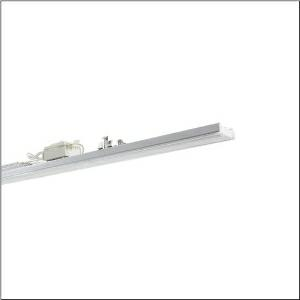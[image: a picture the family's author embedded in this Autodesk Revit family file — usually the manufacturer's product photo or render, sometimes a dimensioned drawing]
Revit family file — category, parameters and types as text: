
# Revit family: licross_r__11_recessed_ho_51tl11dn4exs_1c00
name_source: partatom
category: Lighting Fixtures
units: mm (PartAtom-declared; Revit-internal decimal feet)

## family parameters
Cut with Voids When Loaded = No
Host = Face
Light Source = No
Part Type = Normal
Room Calculation Point = No
Round Connector Dimension = Use Diameter
Shared = No

## types (1)
- --- (1 x LED, 14000 lm, 76.8 W, 4000K)
    Apparent Load = 77 VA
    CIE Flux Codes = 87 95 99 100 100
    Color Rendering = 80
    Color Temperature = 4000K
    Default Elevation = 1800 mm
    Description = Licross® 11 Recessed HO, luminaire insert, of sheet steel, coil coated, white, length: 1.500mm, width: 66mm, height: 67mm, LED rated luminous flux: 14.000lm, light colour: 840, control gear: DALI 2, with plug, 5-pole, with phase selection, mains connection: 220..240V, AC, 50/60Hz, rated input power: 77W, halogen-free wiring, primary light control with lens, of plastic, primary optical cover: cover, of PMMA, light emission: direct distribution, primary light characteristic: symmetric, protection rating (complete): IP40, insulation class (complete): insulation class I (protective earthing), certification: CE, ENEC, VDE, UKCA, protection symbol: D if used in an environment without relevant dust loads with corresponding accessories, impact resistance: IK06, permissible ambient temperature for indoor applications: -25..+30°C, corresponds to IFS (International Featured Standards) requirements for safety and quality in the food industry, reducing of maximum allowable ambient temperature of 5°C with ceiling mounting, LABS conformity tested according to VDMA 24364:2018-05, packaging unit: 1 piece
    Height = 58 mm
    Lamp = 1 x LED
    Lamp Light Flux = 14000 lm
    Lamp Power = 76.8 W
    Lamp count = 1
    Length = 1500 mm
    Luminous efficacy = 182 lm/W
    Manufacturer = Siteco
    ModVariant = No
    Model = 51TL11DN4EXS
    Mounting Place = Ceiling
    Mounting Type = Pendant
    Number of Poles = 1
    OnlyDefault = Yes
    Power Factor = 1
    Product Name = Licross® 11 Recessed HO
    Product group = luminaire insert
    ProductGroupID = 902
    Protection Class = Protection class I
    Protection Degree = IP 40
    RLX_Detail_Level = 1
    RLX_Emergency_Light_Flux = 0 lm
    RLX_Emergency_Type = 0
    RLX_Emergency_Type_DB = No
    RlxData = <blob elided: 24553 chars, md5=e88012f4>
    Socket = socket
    Standby Power = 0 W
    System Light Flux = 14000 lm
    System Power = 77 W
    Type Comments = factory setting: luminous flux: 100 % | dim-lin: 254 | 522 mA
    Type Image = l_1296930.jpg
    URL = http://relux.com
    VarID = @adj_098948
    Voltage = 0 V
    Weight = 0.00 kg
    Width = 66 mm

## geometry (parser evidence)
native form markers: Blend x4, Sweep x12
no freeform markers — native parametric forms only
